# Revit family: Bath-Freestanding-Filler_Drain-KOHLER-Volute-K-99311T_1
name_source: partatom
category: Plumbing Fixtures
units: mm (PartAtom-declared; Revit-internal decimal feet)

## family parameters
Cut with Voids When Loaded = No
Host = Face
OmniClass Number = 23.31.15.00
OmniClass Title = Bathtubs
Part Type = Normal
Room Calculation Point = No
Round Connector Dimension = Use Diameter
Shared = No

## types (2) — shared parameters
ADA Compliant = No
Assembly Code = D2010500
CW Connection = Yes
Cold Water Inlet = Cold Water Inlet
Date Modified = 02/27/2023
Default Elevation = 0"
Drain Included = Yes
Finish = KOHLER-Cast_Iron-0-White
HW Connection = No
Height = 20 7/8"
Hot Water Inlet = Hot Water Inlet
Length = 66 15/16"
Manufacturer = Kohler Co.
Master Format 2014 = 22 41 19
Master Format 2014 Name = Residential Bathtubs
Material = Cast Iron
Product Name = Volute
URL = http://www.kohler.com.cn
Vent Connection = No
Waste Connection = Yes
Waste Water Outlet = Waste Water Outlet
WaterSense Certified = No
Width = 31 1/2"

## per-type parameters (varying)
| type | Description | Grip Rail | Model | Type |
| With Grip Rail, 0-White | 1.6M Freestanding Bath With Grip Rail Hole | Yes | K-99311T-FDGR-0 | 2 |
| Without Grip Rail, 0-White | 1.7M Freestanding Bath With Filler Drain | No | K-99311T-FD-0 | 1 |

## geometry (parser evidence)
native form markers: Sweep x5
no freeform markers — native parametric forms only
